# Revit family: 603-A-4100-DN300
name_source: partatom
category: Pipe Accessories
units: mm (PartAtom-declared; Revit-internal decimal feet)

## family parameters
Always vertical = Yes
Cut with Voids When Loaded = No
Part Type = Valve - Breaks Into
Round Connector Dimension = Use Diameter
Shared = No
Work Plane-Based = No

## types (3) — shared parameters
Bolt_ref = 154 mm  [stored 0.505249 ft]
Bolt_width = 20 mm  [stored 0.0656168 ft]
Bottm_cut = 184 mm
Bottm_height = 8 mm  [stored 0.0262467 ft]
Bottom_Flange_Thicckness = 12 mm  [stored 0.0393701 ft]
D2 = 146 mm
D3 = 175 mm
D4 = 212 mm  [stored 0.695538 ft]
DN300_ 324-350 = 603-350-000-4100
DN300_301- 327 = 603-327-002-4100
DN300_301-327 = 603-327-000-4100
Description_ = AVK UNIVERSAL SUPA® FLANGE ADAPTOR
H1 = 35 mm  [stored 0.114829 ft]
ID = 120 mm  [stored 0.393701 ft]
L = 178 mm  [stored 0.58399 ft]
L1 = 61 mm  [stored 0.200131 ft]
L3 = 112 mm  [stored 0.367454 ft]
Length = 119 mm  [stored 0.39042 ft]
Nomianal_Diameter(DN) = 300 mm  [stored 0.984252 ft]
Nut = 10 mm  [stored 0.0328084 ft]
PCD = 400 mm  [stored 1.31234 ft]
Rib_Thickness = 5 mm  [stored 0.0164042 ft]
Rib_length = 32 mm  [stored 0.104987 ft]
S = 450 mm  [stored 1.47638 ft]
Search_table = 603-A-4100-DN300
URL product pages = https://www.avkvalves.com
Washer = 3 mm  [stored 0.00984252 ft]
Washer_ref = 144 mm  [stored 0.472441 ft]

## per-type parameters (varying)
| type | D | Rib_width |
| 603-327-000-4100_DN300 | 242 mm | 480 mm  [stored 1.5748 ft] |
| 603-327-002-4100_DN300 | 229 mm  [stored 0.751312 ft] | 450 mm  [stored 1.47638 ft] |
| 603-350-000-4100_DN300 | 242 mm | 480 mm  [stored 1.5748 ft] |

note: [stored X ft] marks values corroborated as IEEE doubles in the binary element streams (Revit-internal decimal feet)

## geometry (parser evidence)
native form markers: Sweep x10
no freeform markers — native parametric forms only
